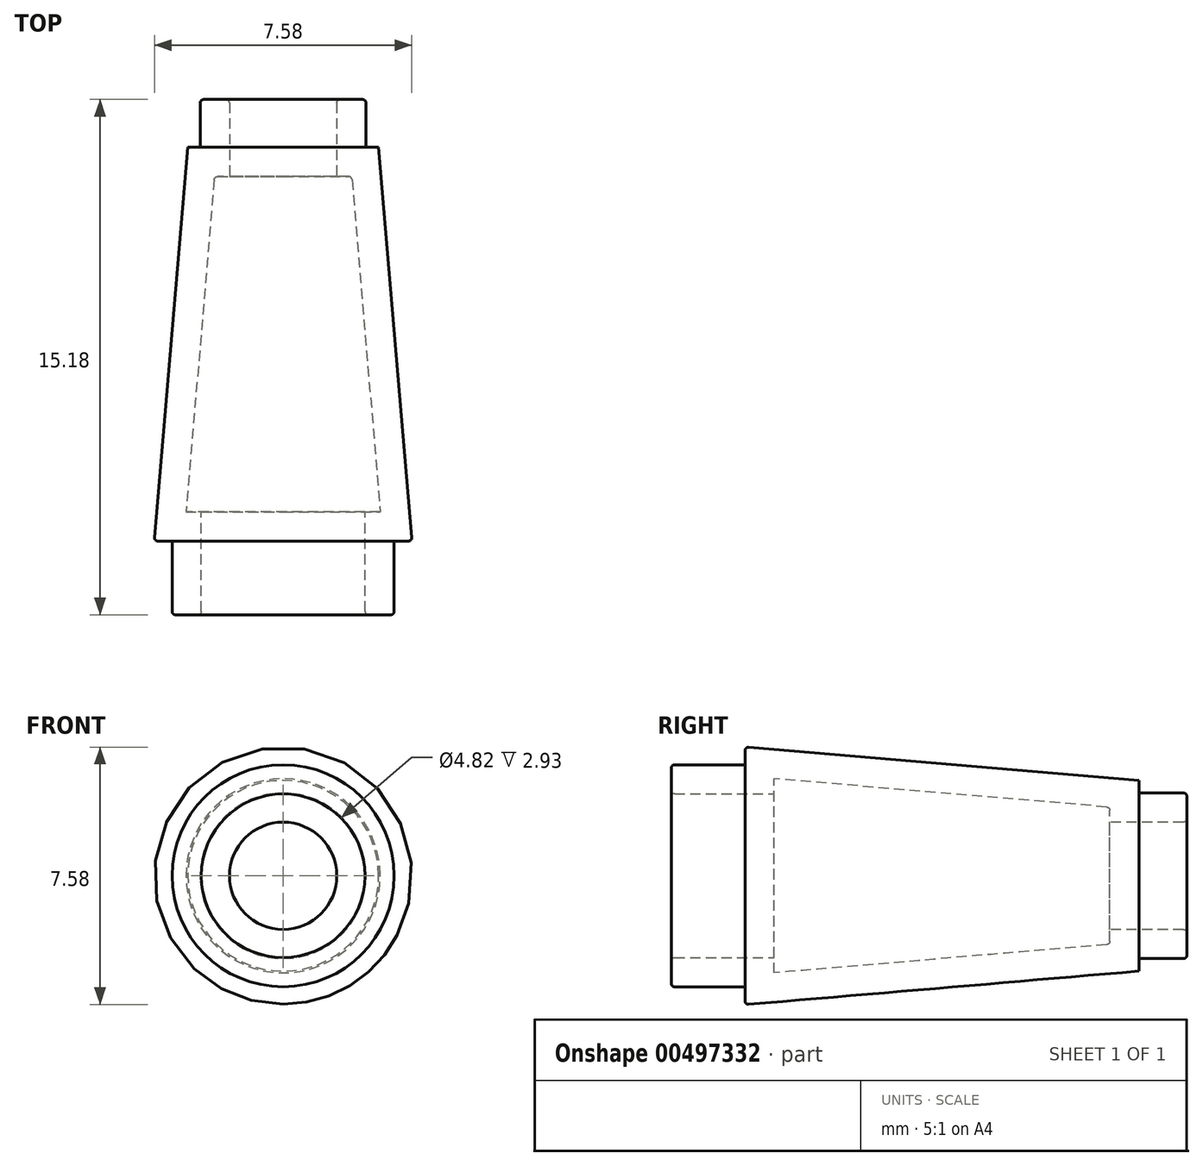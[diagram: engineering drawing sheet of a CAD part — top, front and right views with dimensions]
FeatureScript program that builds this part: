
annotation { "Feature Type Name" : "Feature", "Feature Type Description" : "" }
export const myFeature = defineFeature(function(context is Context, id is Id, definition is map)
    precondition{}
    {
        {
            var Q0;
            Q0=qCreatedBy(makeId("Front.planeOp"),FACE);
            var sketch = newSketch(context, id + "F0", { "sketchPlane" : qUnion([Q0])});
            skCircle(sketch, "E0", {"center": v(0, 0) * mm, "radius": 3.8 * mm});
            skSolve(sketch);
        }
        {
            var Q0;
            Q0=makeQuery(id+"F0.imprint","IMPRINT",FACE,{"disambiguationData":[TD([[makeQuery(id+"F0.imprint","IMPRINT",EDGE,{"derivedFrom":sQuery(id+"F0.wireOp",EDGE,"E0")}),1.0]])]});
            extrude(context, id + "F1", {"entities" : qUnion([Q0]), "oppositeDirection" : true, "depth" : 11.6 * mm});
        }
        {
            var Q0;
            Q0=makeQuery(id+"F1.opExtrude","CAP_FACE",FACE,{"disambiguationData":[OSD([sQuery(id+"F0.wireOp",EDGE,"E0")])],"isStart":false});
            var sketch = newSketch(context, id + "F2", { "sketchPlane" : qUnion([Q0])});
            skCircle(sketch, "E1", {"center": v(0, 0) * mm, "radius": 2.8 * mm});
            skSolve(sketch);
        }
        {
            var Q1;
            Q1=makeQuery(id+"F2.imprint","IMPRINT",FACE,{"disambiguationData":[TD([[makeQuery(id+"F2.imprint","IMPRINT",EDGE,{"derivedFrom":sQuery(id+"F2.wireOp",EDGE,"E1")}),1.0]])]});
            var Q2;
            Q2=makeQuery(id+"F1.opExtrude","CAP_FACE",FACE,{"disambiguationData":[OSD([sQuery(id+"F0.wireOp",EDGE,"E0")])],"isStart":true});
            loft(context, id + "F3", {"operationType" : NewBodyOperationType.INTERSECT, "sheetProfilesArray" : [{ "sheetProfileEntities" : qUnion([Q1]) }, { "sheetProfileEntities" : qUnion([Q2]) }]});
        }
        {
            var Q0;
            Q0=makeQuery(id+"F1.opExtrude","CAP_FACE",FACE,{"disambiguationData":[OSD([sQuery(id+"F0.wireOp",EDGE,"E0")])],"isStart":false});
            var sketch = newSketch(context, id + "F4", { "sketchPlane" : qUnion([Q0])});
            skCircle(sketch, "E2", {"center": v(0, 0) * mm, "radius": 2.44 * mm});
            skSolve(sketch);
        }
        {
            var Q0;
            Q0 = qSketchRegion(id + "F4", true);
            extrude(context, id + "F5", {"entities" : qUnion([Q0]), "operationType" : NewBodyOperationType.ADD, "depth" : 1.41 * mm});
        }
        {
            var Q0;
            Q0=makeQuery(id+"F1.opExtrude","CAP_FACE",FACE,{"disambiguationData":[OSD([sQuery(id+"F0.wireOp",EDGE,"E0")])],"isStart":true});
            var sketch = newSketch(context, id + "F6", { "sketchPlane" : qUnion([Q0])});
            skCircle(sketch, "E3", {"center": v(0, 0) * mm, "radius": 3.27 * mm});
            skSolve(sketch);
        }
        {
            var Q0;
            Q0=makeQuery(id+"F6.imprint","IMPRINT",FACE,{"disambiguationData":[TD([[makeQuery(id+"F6.imprint","IMPRINT",EDGE,{"derivedFrom":sQuery(id+"F6.wireOp",EDGE,"E3")}),1.0]])]});
            extrude(context, id + "F7", {"entities" : qUnion([Q0]), "operationType" : NewBodyOperationType.ADD, "depth" : 2.17 * mm});
        }
        {
            var Q0;
            Q0=makeQuery(id+"F5.opExtrude","CAP_FACE",FACE,{"disambiguationData":[OSD([sQuery(id+"F4.wireOp",EDGE,"E2")])],"isStart":false});
            var Q1;
            Q1=makeQuery(id+"F7.opExtrude","CAP_FACE",FACE,{"disambiguationData":[OSD([sQuery(id+"F6.wireOp",EDGE,"E3")])],"isStart":false});
            shell(context, id + "F8", {"entities" : qUnion([Q0, Q1]), "thickness" : 0.86 * mm});
        }
        {
            var Q0;
            Q0=makeQuery(id+"F7.opExtrude","CAP_EDGE",EDGE,{"disambiguationData":[OSD([sQuery(id+"F6.wireOp",EDGE,"E3")])],"isStart":true});
            var Q1;
            Q1=makeQuery(id+"F3.boolean.opBoolean","COPY",EDGE,{"derivedFrom":makeQuery(id+"F3.boolean.toolComplement.opBoolean","COPY",EDGE,{"derivedFrom":makeQuery(id+"F3.opLoft","MID_CAP_EDGE",EDGE,{"disambiguationData":[OSD([sQuery(id+"F2.wireOp",EDGE,"E1")])],"capPos":0.0})})});
            var Q2;
            Q2=makeQuery(id+"F7.opExtrude","CAP_EDGE",EDGE,{"disambiguationData":[OSD([sQuery(id+"F6.wireOp",EDGE,"E3")])],"isStart":false});
            var Q3;
            {var subQ0=sQuery(id+"F0.wireOp",EDGE,"E0");Q3=makeQuery(id+"F3.boolean.opBoolean","MERGE",EDGE,{"derivedFrom":[makeQuery(id+"F1.opExtrude","CAP_EDGE",EDGE,{"disambiguationData":[OSD([subQ0])],"isStart":true}),makeQuery(id+"F3.boolean.toolComplement.opBoolean","COPY",EDGE,{"derivedFrom":makeQuery(id+"F3.opLoft","MID_CAP_EDGE",EDGE,{"disambiguationData":[OSD([subQ0,sQuery(id+"F2.wireOp",EDGE,"E1")])],"capPos":1.0})})]});}
            var Q4;
            Q4=makeQuery(id+"F5.opExtrude","CAP_EDGE",EDGE,{"disambiguationData":[OSD([sQuery(id+"F4.wireOp",EDGE,"E2")])],"isStart":false});
            var Q5;
            {var subQ0=sQuery(id+"F6.wireOp",EDGE,"E3");Q5=makeQuery(id+"F8.opShell","OFFSET_EDGE",EDGE,{"disambiguationData":[OSD([subQ0]),TDD([makeQuery(id+"F7.opExtrude","CAP_EDGE",EDGE,{"disambiguationData":[OSD([subQ0])],"isStart":true})])]});}
            var Q6;
            {var subQ0=sQuery(id+"F6.wireOp",EDGE,"E3");Q6=makeQuery(id+"F8.opShell","OFFSET_EDGE",EDGE,{"disambiguationData":[OSD([subQ0]),TDD([makeQuery(id+"F7.opExtrude","CAP_EDGE",EDGE,{"disambiguationData":[OSD([subQ0])],"isStart":false})])]});}
            var Q7;
            Q7=makeQuery(id+"F5.opExtrude","CAP_EDGE",EDGE,{"disambiguationData":[OSD([sQuery(id+"F4.wireOp",EDGE,"E2")])],"isStart":true});
            var Q8;
            Q8=makeQuery(id+"F8.opShell","OFFSET_EDGE",EDGE,{"disambiguationData":[OSD([sQuery(id+"F0.wireOp",EDGE,"E0"),sQuery(id+"F2.wireOp",EDGE,"E1")])]});
            var Q9;
            Q9=makeQuery(id+"F8.opShell","OFFSET_EDGE",EDGE,{"disambiguationData":[OSD([sQuery(id+"F2.wireOp",EDGE,"E1")])]});
            var Q10;
            {var subQ0=sQuery(id+"F4.wireOp",EDGE,"E2");Q10=makeQuery(id+"F8.opShell","OFFSET_EDGE",EDGE,{"disambiguationData":[OSD([subQ0]),TDD([makeQuery(id+"F5.opExtrude","CAP_EDGE",EDGE,{"disambiguationData":[OSD([subQ0])],"isStart":false})])]});}
            var Q11;
            {var subQ0=sQuery(id+"F4.wireOp",EDGE,"E2");Q11=makeQuery(id+"F8.opShell","OFFSET_EDGE",EDGE,{"disambiguationData":[OSD([subQ0]),TDD([makeQuery(id+"F5.opExtrude","CAP_EDGE",EDGE,{"disambiguationData":[OSD([subQ0])],"isStart":true})])]});}
            fillet(context, id + "F9", {"entities" : qUnion([Q0, Q1, Q2, Q3, Q4, Q5, Q6, Q7, Q8, Q9, Q10, Q11]), "radius" : 0.1 * mm, "tangentPropagation" : true, "allowEdgeOverflow" : false});
        }
    });
